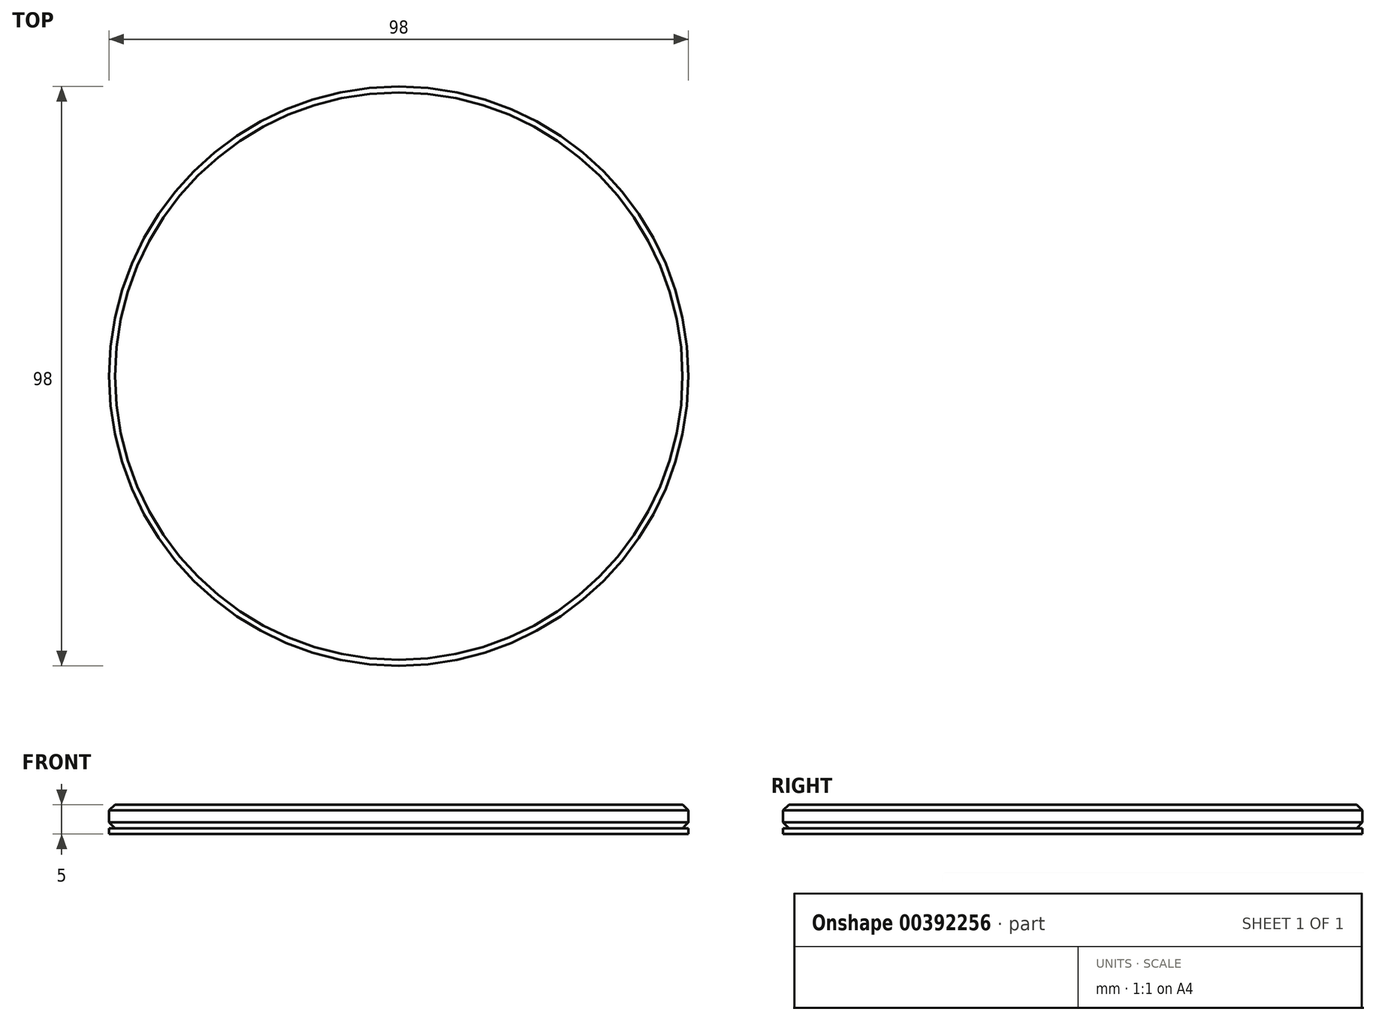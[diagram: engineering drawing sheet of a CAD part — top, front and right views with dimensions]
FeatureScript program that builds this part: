
annotation { "Feature Type Name" : "Feature", "Feature Type Description" : "" }
export const myFeature = defineFeature(function(context is Context, id is Id, definition is map)
    precondition{}
    {
        {
            var Q0;
            Q0=qCreatedBy(makeId("Top.planeOp"),FACE);
            var sketch = newSketch(context, id + "F0", { "sketchPlane" : qUnion([Q0])});
            skCircle(sketch, "E0", {"center": v(0, 0) * mm, "radius": 49 * mm});
            skSolve(sketch);
        }
        {
            var Q0;
            Q0 = qSketchRegion(id + "F0", true);
            extrude(context, id + "F1", {"entities" : qUnion([Q0]), "depth" : 4 * mm, "offsetDistance" : 25 * mm});
        }
        {
            var Q0;
            Q0=makeQuery(id+"F1.opExtrude","CAP_EDGE",EDGE,{"disambiguationData":[OSD([sQuery(id+"F0.wireOp",EDGE,"E0")])],"isStart":false});
            var Q1;
            Q1=makeQuery(id+"F1.opExtrude","CAP_EDGE",EDGE,{"disambiguationData":[OSD([sQuery(id+"F0.wireOp",EDGE,"E0")])],"isStart":true});
            chamfer(context, id + "F2", {"entities" : qUnion([Q0, Q1]), "width" : 1 * mm, "tangentPropagation" : true});
        }
        {
            var Q0;
            Q0=makeQuery(id+"F1.opExtrude","CAP_FACE",FACE,{"disambiguationData":[OSD([sQuery(id+"F0.wireOp",EDGE,"E0")])],"isStart":true});
            var sketch = newSketch(context, id + "F3", { "sketchPlane" : qUnion([Q0])});
            skCircle(sketch, "E1.0", {"center": v(0, 0) * mm, "radius": 49 * mm});
            skSolve(sketch);
        }
        {
            var Q0;
            Q0 = qSketchRegion(id + "F3", true);
            extrude(context, id + "F4", {"entities" : qUnion([Q0]), "depth" : 1 * mm, "offsetDistance" : 25 * mm});
        }
    });
